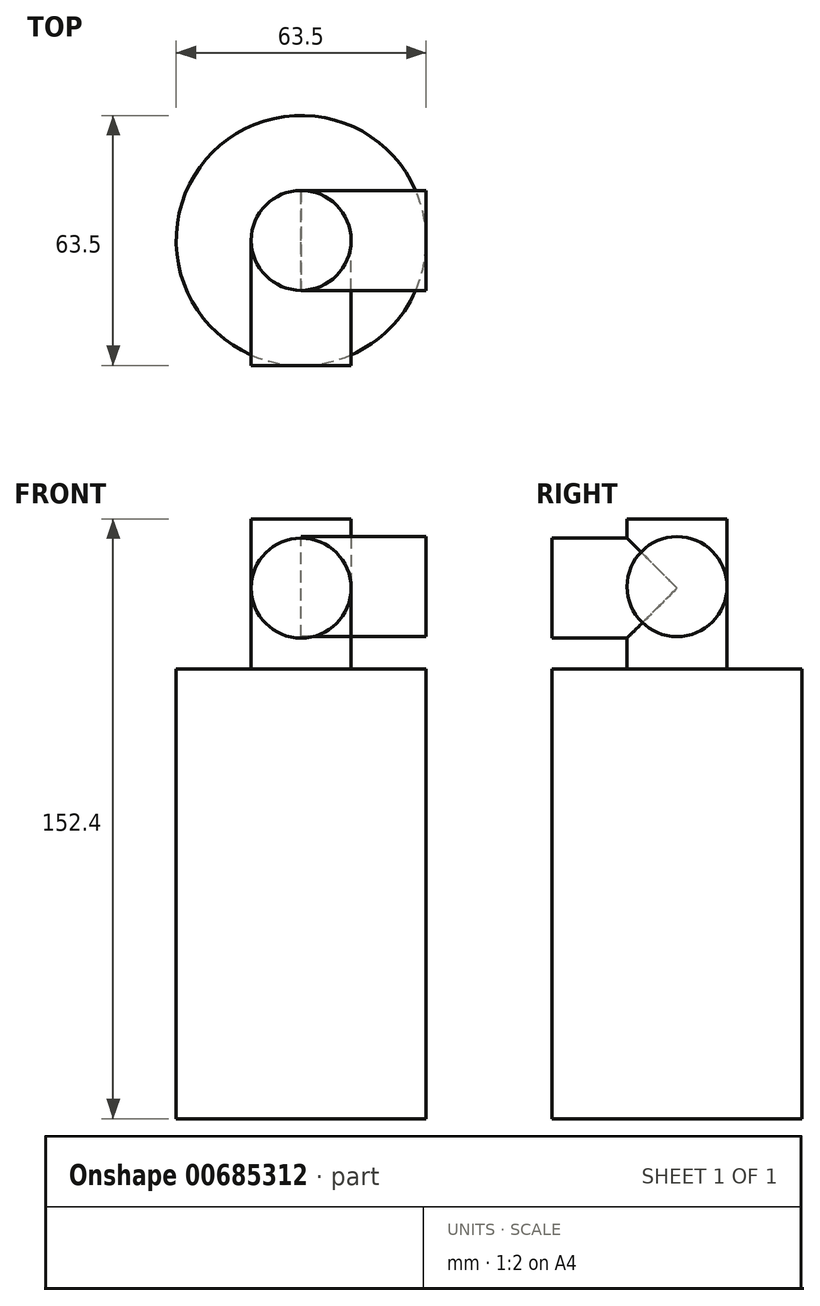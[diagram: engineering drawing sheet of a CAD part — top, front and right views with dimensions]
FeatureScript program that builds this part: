
annotation { "Feature Type Name" : "Feature", "Feature Type Description" : "" }
export const myFeature = defineFeature(function(context is Context, id is Id, definition is map)
    precondition{}
    {
        {
            var Q0;
            Q0=qCreatedBy(makeId("Top.planeOp"),FACE);
            var sketch = newSketch(context, id + "F0", { "sketchPlane" : qUnion([Q0])});
            skCircle(sketch, "E0", {"center": v(0, 0) * mm, "radius": 31.75 * mm});
            skSolve(sketch);
        }
        {
            var Q0;
            Q0=qSketchRegion(id+"F0",true);
            extrude(context, id + "F1", {"entities" : qUnion([Q0]), "depth" : 114.3 * mm, "offsetDistance" : 25.4 * mm});
        }
        {
            var Q0;
            Q0=makeQuery(id+"F1.opExtrude","CAP_FACE",FACE,{"disambiguationData":[OSD([sQuery(id+"F0.wireOp",EDGE,"E0")])],"isStart":false});
            var sketch = newSketch(context, id + "F2", { "sketchPlane" : qUnion([Q0])});
            skCircle(sketch, "E1", {"center": v(0, 0) * mm, "radius": 12.7 * mm});
            skSolve(sketch);
        }
        {
            var Q0;
            Q0=qSketchRegion(id+"F2",true);
            extrude(context, id + "F3", {"entities" : qUnion([Q0]), "operationType" : NewBodyOperationType.ADD, "depth" : 38.1 * mm, "offsetDistance" : 25.4 * mm});
        }
        {
            var Q0;
            Q0=qCreatedBy(makeId("Front.planeOp"),FACE);
            var sketch = newSketch(context, id + "F4", { "sketchPlane" : qUnion([Q0])});
            skCircle(sketch, "E2", {"center": v(0, 134.8) * mm, "radius": 12.7 * mm});
            skSolve(sketch);
        }
        {
            var Q0;
            Q0=qSketchRegion(id+"F4",true);
            extrude(context, id + "F5", {"entities" : qUnion([Q0]), "operationType" : NewBodyOperationType.ADD, "depth" : 31.75 * mm, "offsetDistance" : 25.4 * mm});
        }
        {
            var Q0;
            Q0=qCreatedBy(makeId("Right.planeOp"),FACE);
            var sketch = newSketch(context, id + "F6", { "sketchPlane" : qUnion([Q0])});
            skCircle(sketch, "E3", {"center": v(0, 135.16) * mm, "radius": 12.7 * mm});
            skSolve(sketch);
        }
        {
            var Q0;
            Q0=qSketchRegion(id+"F6",true);
            extrude(context, id + "F7", {"entities" : qUnion([Q0]), "depth" : 31.75 * mm, "offsetDistance" : 25.4 * mm});
        }
    });
